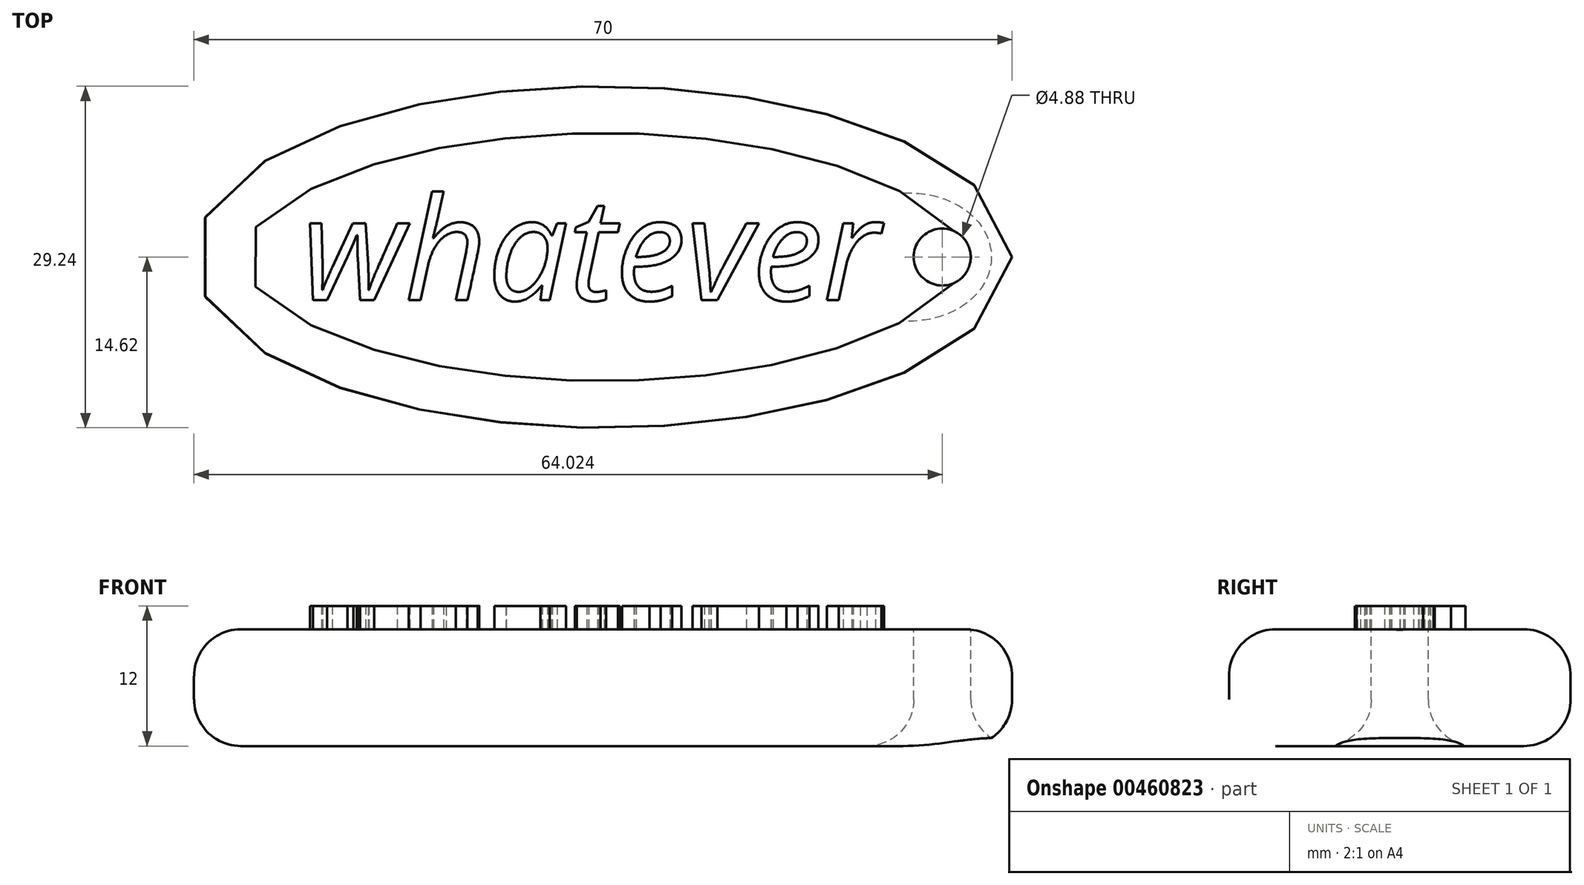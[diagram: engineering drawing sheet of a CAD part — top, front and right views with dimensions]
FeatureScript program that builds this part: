
annotation { "Feature Type Name" : "Feature", "Feature Type Description" : "" }
export const myFeature = defineFeature(function(context is Context, id is Id, definition is map)
    precondition{}
    {
        {
            var Q0;
            Q0=qCreatedBy(makeId("Top.planeOp"),FACE);
            var sketch = newSketch(context, id + "F0", { "sketchPlane" : qUnion([Q0])});
            skLineSegment(sketch, "E0", {"start": v(0, 0) * mm, "end": v(35, 0) * mm});
            skEllipse(sketch, "E1", {"center": v(0, 0) * mm, "majorRadius": 35 * mm, "minorRadius": 14.62 * mm, "majorAxis": v(1, 0)});
            skSolve(sketch);
        }
        {
            var Q0;
            Q0 = qSketchRegion(id + "F0", true);
            extrude(context, id + "F1", {"entities" : qUnion([Q0]), "depth" : 10 * mm});
        }
        {
            var Q0;
            Q0=makeQuery(id+"F1.opExtrude","CAP_FACE",FACE,{"disambiguationData":[OSD([sQuery(id+"F0.wireOp",EDGE,"E1")])],"isStart":false});
            var sketch = newSketch(context, id + "F2", { "sketchPlane" : qUnion([Q0])});
            skText(sketch, "E2", { "text": "whatever", "fontName": "OpenSans-Italic.ttf"});
            const initialGuessF2  = {"E2": [-0.02578, -0.0037, 1, 0, 0.00884]};
            skSetInitialGuess(sketch, initialGuessF2);
            skSolve(sketch);
        }
        {
            var Q0;
            Q0 = qSketchRegion(id + "F2", true);
            extrude(context, id + "F3", {"entities" : qUnion([Q0]), "operationType" : NewBodyOperationType.ADD, "depth" : 2 * mm});
        }
        {
            var Q0;
            {var subQ0=sQuery(id+"F0.wireOp",EDGE,"E1");Q0=makeQuery(id+"F3.boolean.opBoolean","SPLIT",FACE,{"disambiguationData":[TD([makeQuery(id+"F1.opExtrude","SWEPT_FACE",FACE,{"disambiguationData":[OSD([subQ0])]})])],"derivedFrom":makeQuery(id+"F1.opExtrude","CAP_FACE",FACE,{"disambiguationData":[OSD([subQ0])],"isStart":false})});}
            var sketch = newSketch(context, id + "F4", { "sketchPlane" : qUnion([Q0])});
            skLineSegment(sketch, "E3", {"start": v(35, 0) * mm, "end": v(23.05, 0) * mm});
            skPoint(sketch, "E3.endSnap0", {"position": v(35, 0) * mm});
            skCircle(sketch, "E4", {"center": v(29.02, 0) * mm, "radius": 2.44 * mm});
            skSolve(sketch);
        }
        {
            var Q0;
            Q0 = qSketchRegion(id + "F4", true);
            extrude(context, id + "F5", {"entities" : qUnion([Q0]), "operationType" : NewBodyOperationType.REMOVE, "oppositeDirection" : true, "depth" : 25 * mm});
        }
        {
            var Q0;
            Q0=makeQuery(id+"F1.opExtrude","CAP_FACE",FACE,{"disambiguationData":[OSD([sQuery(id+"F0.wireOp",EDGE,"E1")])],"isStart":true});
            fillet(context, id + "F6", {"entities" : qUnion([Q0]), "radius" : 4 * mm, "tangentPropagation" : true, "allowEdgeOverflow" : false});
        }
        {
            var Q0;
            Q0=makeQuery(id+"F1.opExtrude","CAP_EDGE",EDGE,{"disambiguationData":[OSD([sQuery(id+"F0.wireOp",EDGE,"E1")])],"isStart":false});
            fillet(context, id + "F7", {"entities" : qUnion([Q0]), "radius" : 4 * mm, "tangentPropagation" : true, "allowEdgeOverflow" : false});
        }
    });
